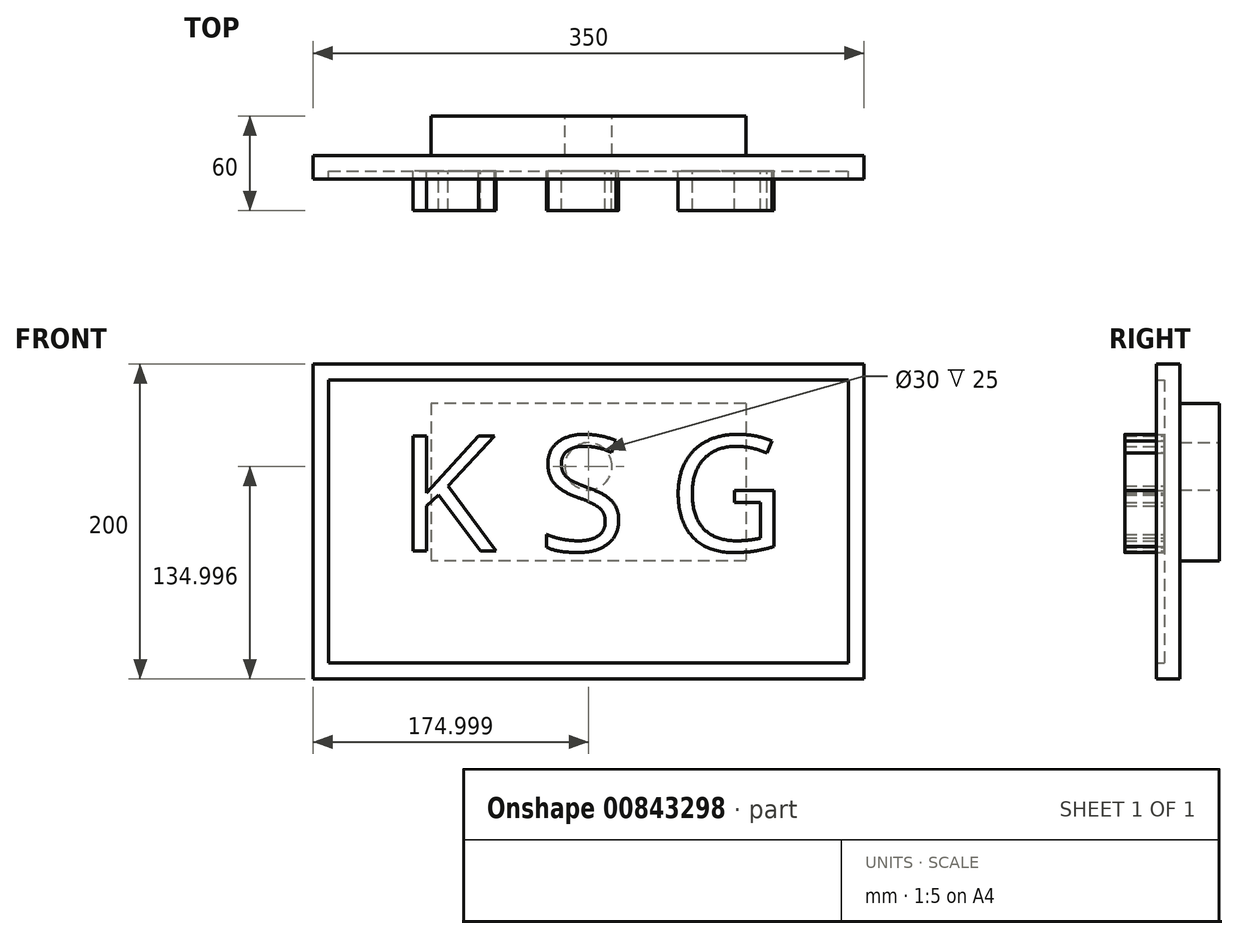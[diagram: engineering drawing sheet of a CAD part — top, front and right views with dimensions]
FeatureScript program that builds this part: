
annotation { "Feature Type Name" : "Feature", "Feature Type Description" : "" }
export const myFeature = defineFeature(function(context is Context, id is Id, definition is map)
    precondition{}
    {
        {
            var Q0;
            Q0=qCreatedBy(makeId("Front.planeOp"),FACE);
            var sketch = newSketch(context, id + "F0", { "sketchPlane" : qUnion([Q0])});
            skLineSegment(sketch, "E0.bottom", {"start": v(-242.82, 141.4) * mm, "end": v(107.18, 141.4) * mm});
            skLineSegment(sketch, "E0.top", {"start": v(-242.82, -58.6) * mm, "end": v(107.18, -58.6) * mm});
            skLineSegment(sketch, "E0.left", {"start": v(-242.82, 141.4) * mm, "end": v(-242.82, -58.6) * mm});
            skLineSegment(sketch, "E0.right", {"start": v(107.18, 141.4) * mm, "end": v(107.18, -58.6) * mm});
            skLineSegment(sketch, "E1.bottom", {"start": v(-232.82, 131.4) * mm, "end": v(97.18, 131.4) * mm});
            skLineSegment(sketch, "E1.top", {"start": v(-232.82, -48.6) * mm, "end": v(97.18, -48.6) * mm});
            skLineSegment(sketch, "E1.left", {"start": v(-232.82, 131.4) * mm, "end": v(-232.82, -48.6) * mm});
            skLineSegment(sketch, "E1.right", {"start": v(97.18, 131.4) * mm, "end": v(97.18, -48.6) * mm});
            skSolve(sketch);
        }
        {
            var Q0;
            Q0=makeQuery(id+"F0.imprint","IMPRINT",FACE,{"disambiguationData":[TD([[makeQuery(id+"F0.imprint","IMPRINT",EDGE,{"derivedFrom":sQuery(id+"F0.wireOp",EDGE,"E1.bottom")}),-1.0]])]});
            extrude(context, id + "F1", {"entities" : qUnion([Q0]), "depth" : 10 * mm, "offsetDistance" : 25 * mm});
        }
        {
            var Q0;
            Q0=makeQuery(id+"F0.imprint","IMPRINT",FACE,{"disambiguationData":[TD([[makeQuery(id+"F0.imprint","IMPRINT",EDGE,{"derivedFrom":sQuery(id+"F0.wireOp",EDGE,"E0.bottom")}),-1.0]])]});
            extrude(context, id + "F2", {"entities" : qUnion([Q0]), "operationType" : NewBodyOperationType.ADD, "depth" : 15 * mm, "offsetDistance" : 25 * mm});
        }
        {
            var Q0;
            {var subQ0=sQuery(id+"F0.wireOp",EDGE,"E1.right");var subQ1=sQuery(id+"F0.wireOp",EDGE,"E1.left");var subQ2=sQuery(id+"F0.wireOp",EDGE,"E1.top");var subQ3=sQuery(id+"F0.wireOp",EDGE,"E1.bottom");Q0=makeQuery(id+"F2.boolean.opBoolean","MERGE",FACE,{"derivedFrom":[makeQuery(id+"F1.opExtrude","CAP_FACE",FACE,{"disambiguationData":[OSD([subQ3,subQ2,subQ1,subQ0])],"isStart":true}),makeQuery(id+"F2.opExtrude","CAP_FACE",FACE,{"disambiguationData":[OSD([sQuery(id+"F0.wireOp",EDGE,"E0.bottom"),sQuery(id+"F0.wireOp",EDGE,"E0.top"),sQuery(id+"F0.wireOp",EDGE,"E0.left"),sQuery(id+"F0.wireOp",EDGE,"E0.right"),subQ3,subQ2,subQ1,subQ0])],"isStart":true})]});}
            var sketch = newSketch(context, id + "F3", { "sketchPlane" : qUnion([Q0])});
            skLineSegment(sketch, "E2.bottom", {"start": v(-32.18, 116.4) * mm, "end": v(167.82, 116.4) * mm});
            skLineSegment(sketch, "E2.top", {"start": v(-32.18, 16.4) * mm, "end": v(167.82, 16.4) * mm});
            skLineSegment(sketch, "E2.left", {"start": v(-32.18, 116.4) * mm, "end": v(-32.18, 16.4) * mm});
            skLineSegment(sketch, "E2.right", {"start": v(167.82, 116.4) * mm, "end": v(167.82, 16.4) * mm});
            skSolve(sketch);
        }
        {
            var Q0;
            Q0 = qSketchRegion(id + "F3", true);
            extrude(context, id + "F4", {"entities" : qUnion([Q0]), "operationType" : NewBodyOperationType.ADD, "depth" : 25 * mm, "offsetDistance" : 25 * mm});
        }
        {
            var Q0;
            Q0=makeQuery(id+"F4.opExtrude","CAP_FACE",FACE,{"disambiguationData":[OSD([sQuery(id+"F3.wireOp",EDGE,"E2.bottom"),sQuery(id+"F3.wireOp",EDGE,"E2.top"),sQuery(id+"F3.wireOp",EDGE,"E2.left"),sQuery(id+"F3.wireOp",EDGE,"E2.right")])],"isStart":false});
            var sketch = newSketch(context, id + "F5", { "sketchPlane" : qUnion([Q0])});
            skCircle(sketch, "E3", {"center": v(67.82, 76.4) * mm, "radius": 15 * mm});
            skSolve(sketch);
        }
        {
            var Q0;
            Q0 = qSketchRegion(id + "F5", true);
            extrude(context, id + "F6", {"entities" : qUnion([Q0]), "operationType" : NewBodyOperationType.REMOVE, "oppositeDirection" : true, "depth" : 25 * mm, "offsetDistance" : 25 * mm});
        }
        {
            var Q0;
            Q0=makeQuery(id+"F1.opExtrude","CAP_FACE",FACE,{"disambiguationData":[OSD([sQuery(id+"F0.wireOp",EDGE,"E1.bottom"),sQuery(id+"F0.wireOp",EDGE,"E1.top"),sQuery(id+"F0.wireOp",EDGE,"E1.left"),sQuery(id+"F0.wireOp",EDGE,"E1.right")])],"isStart":false});
            var sketch = newSketch(context, id + "F7", { "sketchPlane" : qUnion([Q0])});
            skText(sketch, "E4", { "text": "K S G", "fontName": "OpenSans-Regular.ttf"});
            const initialGuessF7  = {"E4": [-0.18917, 0.02266, 1, 0, 0.07364]};
            skSetInitialGuess(sketch, initialGuessF7);
            skSolve(sketch);
        }
        {
            var Q0;
            Q0 = qSketchRegion(id + "F7", true);
            extrude(context, id + "F8", {"entities" : qUnion([Q0]), "operationType" : NewBodyOperationType.ADD, "depth" : 25 * mm, "offsetDistance" : 25 * mm});
        }
    });
